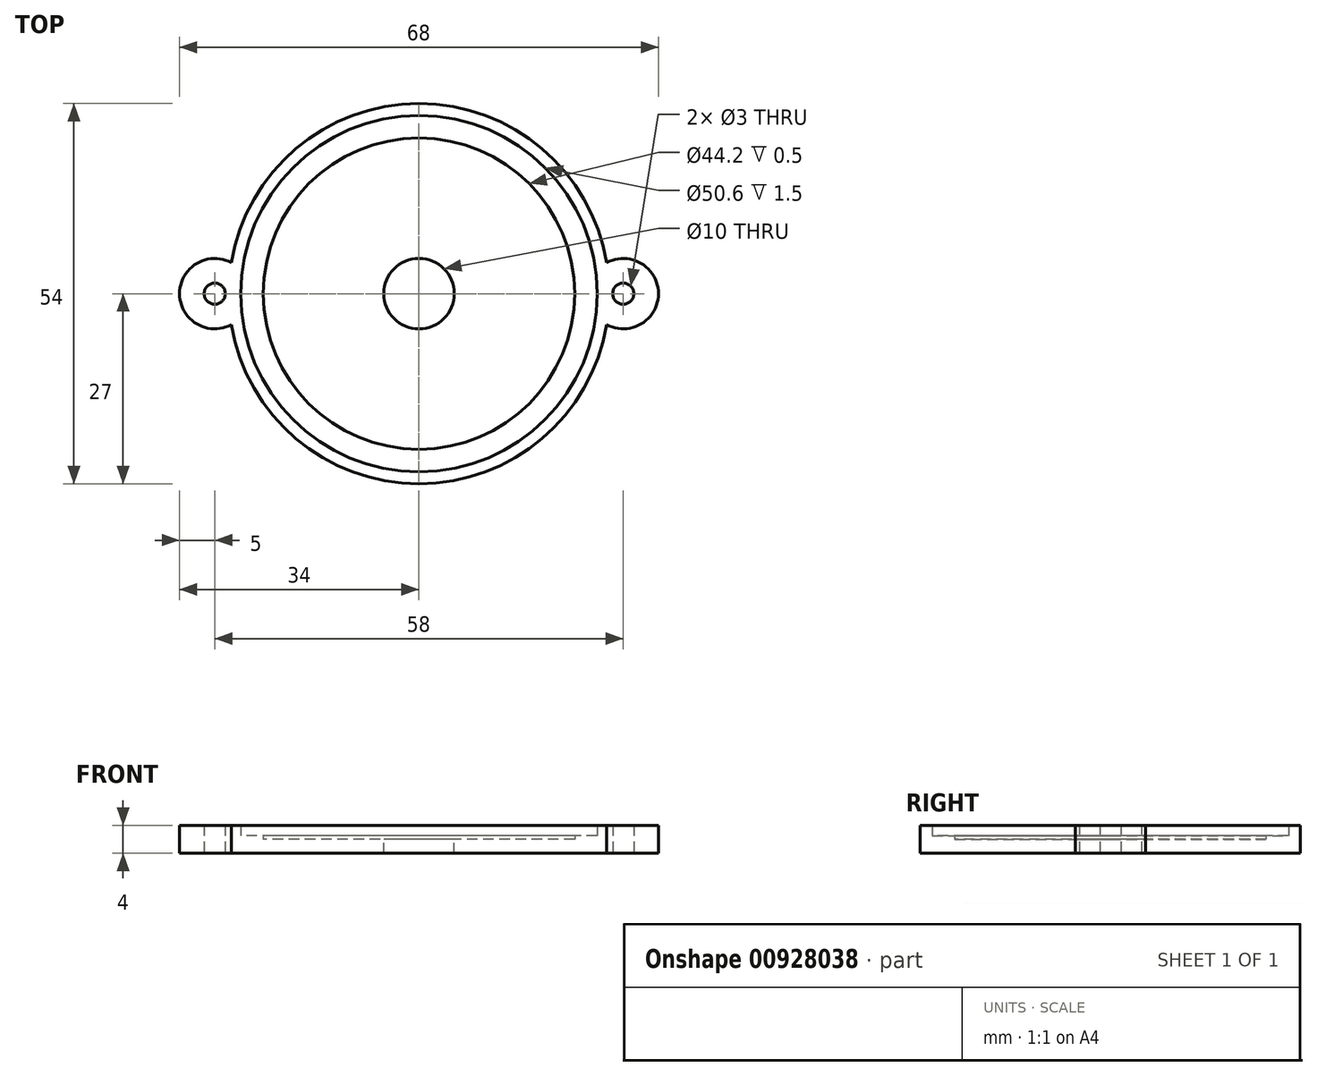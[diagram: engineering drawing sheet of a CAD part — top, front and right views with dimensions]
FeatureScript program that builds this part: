
annotation { "Feature Type Name" : "Feature", "Feature Type Description" : "" }
export const myFeature = defineFeature(function(context is Context, id is Id, definition is map)
    precondition{}
    {
        {
            var Q0;
            Q0=qCreatedBy(makeId("Top.planeOp"),FACE);
            var sketch = newSketch(context, id + "F0", { "sketchPlane" : qUnion([Q0])});
            skCircle(sketch, "E0", {"center": v(0, 0) * mm, "radius": 27 * mm});
            skCircle(sketch, "E1", {"center": v(29, 0) * mm, "radius": 5 * mm});
            skCircle(sketch, "E2", {"center": v(29, 0) * mm, "radius": 1.5 * mm});
            skCircle(sketch, "E3.1.0", {"center": v(-29, 0) * mm, "radius": 5 * mm});
            skCircle(sketch, "E3.1.1", {"center": v(-29, 0) * mm, "radius": 1.5 * mm});
            skSolve(sketch);
        }
        {
            var Q0;
            Q0=makeQuery(id+"F0.imprint","IMPRINT",FACE,{"disambiguationData":[TD([[makeQuery(id+"F0.imprint","IMPRINT",EDGE,{"derivedFrom":sQuery(id+"F0.wireOp",EDGE,"E3.1.1")}),-1.0]])]});
            var Q1;
            Q1=makeQuery(id+"F0.imprint","IMPRINT",FACE,{"disambiguationData":[TD([[makeQuery(id+"F0.imprint","IMPRINT",EDGE,{"derivedFrom":sQuery(id+"F0.wireOp",EDGE,"E2")}),-1.0]])]});
            extrude(context, id + "F1", {"entities" : qUnion([Q0, Q1]), "depth" : 4 * mm, "offsetDistance" : 25 * mm});
        }
        {
            var Q0;
            {var subQ0=sQuery(id+"F0.wireOp",EDGE,"E3.1.0");var subQ1=sQuery(id+"F0.wireOp",EDGE,"E0");var subQ2=makeQuery(id+"F0.imprint","INTERSECT",VERTEX,{"disambiguationData":[OD(0.0)],"derivedFrom":[subQ1,subQ0]});Q0=makeQuery(id+"F0.imprint","IMPRINT",FACE,{"disambiguationData":[TD([[makeQuery(id+"F0.imprint","IMPRINT",EDGE,{"disambiguationData":[TD([[subQ2,-1.0]])],"derivedFrom":subQ1}),1.0]])]});}
            var Q1;
            {var subQ0=sQuery(id+"F0.wireOp",EDGE,"E1");var subQ1=sQuery(id+"F0.wireOp",EDGE,"E0");var subQ2=makeQuery(id+"F0.imprint","INTERSECT",VERTEX,{"disambiguationData":[OD(0.0)],"derivedFrom":[subQ1,subQ0]});Q1=makeQuery(id+"F0.imprint","IMPRINT",FACE,{"disambiguationData":[TD([[makeQuery(id+"F0.imprint","IMPRINT",EDGE,{"disambiguationData":[TD([[subQ2,1.0]])],"derivedFrom":subQ1}),1.0]])]});}
            var Q2;
            {var subQ0=sQuery(id+"F0.wireOp",EDGE,"E3.1.0");var subQ1=sQuery(id+"F0.wireOp",EDGE,"E0");var subQ2=makeQuery(id+"F0.imprint","INTERSECT",VERTEX,{"disambiguationData":[OD(0.0)],"derivedFrom":[subQ1,subQ0]});Q2=makeQuery(id+"F0.imprint","IMPRINT",FACE,{"disambiguationData":[TD([[makeQuery(id+"F0.imprint","IMPRINT",EDGE,{"disambiguationData":[TD([[subQ2,1.0]])],"derivedFrom":subQ1}),1.0]])]});}
            extrude(context, id + "F2", {"entities" : qUnion([Q0, Q1, Q2]), "depth" : 2 * mm, "offsetDistance" : 25 * mm});
        }
        {
            var Q0;
            Q0=makeQuery(id+"F2.opExtrude","CAP_FACE",FACE,{"disambiguationData":[OSD([sQuery(id+"F0.wireOp",EDGE,"E0")])],"isStart":false});
            var sketch = newSketch(context, id + "F3", { "sketchPlane" : qUnion([Q0])});
            skCircle(sketch, "E4", {"center": v(0, 0) * mm, "radius": 22.1 * mm});
            skSolve(sketch);
        }
        {
            var Q0;
            Q0=makeQuery(id+"F3.imprint","IMPRINT",FACE,{"disambiguationData":[TD([[makeQuery(id+"F3.imprint","IMPRINT",EDGE,{"derivedFrom":sQuery(id+"F3.wireOp",EDGE,"E4")}),-1.0]])]});
            extrude(context, id + "F4", {"entities" : qUnion([Q0]), "operationType" : NewBodyOperationType.ADD, "depth" : 0.5 * mm, "offsetDistance" : 25 * mm});
        }
        {
            var Q0;
            Q0=makeQuery(id+"F4.opExtrude","CAP_FACE",FACE,{"disambiguationData":[OSD([sQuery(id+"F0.wireOp",EDGE,"E0"),sQuery(id+"F3.wireOp",EDGE,"E4")])],"isStart":false});
            var sketch = newSketch(context, id + "F5", { "sketchPlane" : qUnion([Q0])});
            skCircle(sketch, "E5", {"center": v(0, 0) * mm, "radius": 25.3 * mm});
            skSolve(sketch);
        }
        {
            var Q0;
            Q0=makeQuery(id+"F5.imprint","IMPRINT",FACE,{"disambiguationData":[TD([[makeQuery(id+"F5.imprint","IMPRINT",EDGE,{"derivedFrom":sQuery(id+"F5.wireOp",EDGE,"E5")}),-1.0]])]});
            extrude(context, id + "F6", {"entities" : qUnion([Q0]), "operationType" : NewBodyOperationType.ADD, "depth" : 1.5 * mm, "offsetDistance" : 25 * mm});
        }
        {
            var Q0;
            Q0=makeQuery(id+"F2.opExtrude","CAP_FACE",FACE,{"disambiguationData":[OSD([sQuery(id+"F0.wireOp",EDGE,"E0")])],"isStart":false});
            var sketch = newSketch(context, id + "F7", { "sketchPlane" : qUnion([Q0])});
            skCircle(sketch, "E6", {"center": v(0, 0) * mm, "radius": 5 * mm});
            skSolve(sketch);
        }
        {
            var Q0;
            Q0=makeQuery(id+"F7.imprint","IMPRINT",FACE,{"disambiguationData":[TD([[makeQuery(id+"F7.imprint","IMPRINT",EDGE,{"derivedFrom":sQuery(id+"F7.wireOp",EDGE,"E6")}),1.0]])]});
            extrude(context, id + "F8", {"entities" : qUnion([Q0]), "operationType" : NewBodyOperationType.REMOVE, "oppositeDirection" : true, "depth" : 25 * mm, "offsetDistance" : 25 * mm});
        }
    });
